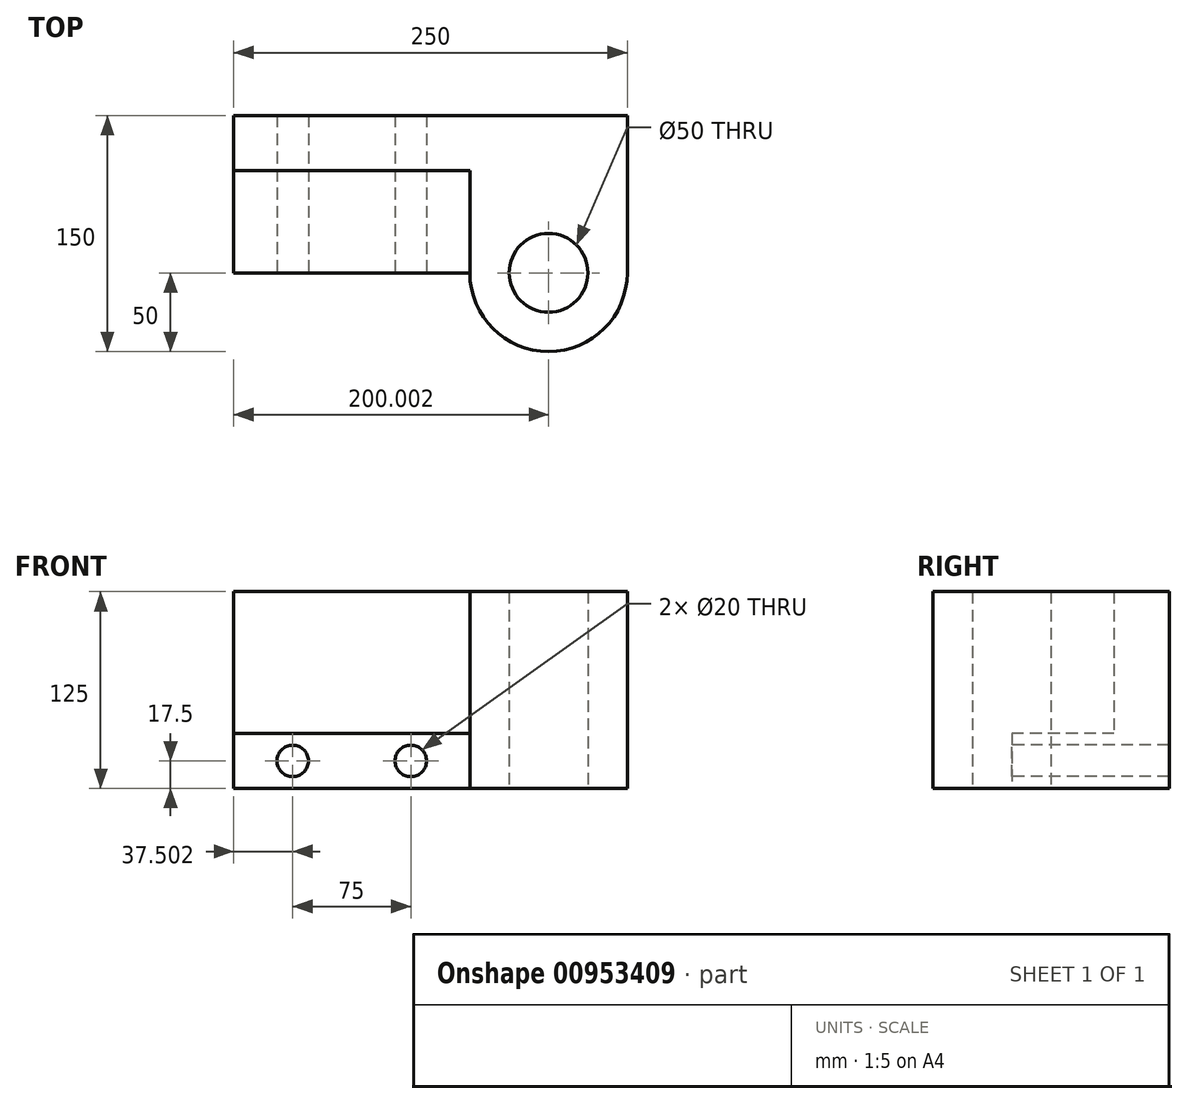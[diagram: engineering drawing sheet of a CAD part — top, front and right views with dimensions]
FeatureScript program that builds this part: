
annotation { "Feature Type Name" : "Feature", "Feature Type Description" : "" }
export const myFeature = defineFeature(function(context is Context, id is Id, definition is map)
    precondition{}
    {
        {
            var Q0;
            Q0=qCreatedBy(makeId("Top.planeOp"),FACE);
            var sketch = newSketch(context, id + "F0", { "sketchPlane" : qUnion([Q0])});
            skLineSegment(sketch, "E0", {"start": v(-118.58, 35) * mm, "end": v(131.42, 35) * mm});
            skLineSegment(sketch, "E1", {"start": v(-118.58, 35) * mm, "end": v(-118.58, 0) * mm});
            skLineSegment(sketch, "E2", {"start": v(-118.58, 0) * mm, "end": v(-118.58, -65) * mm});
            skLineSegment(sketch, "E3", {"start": v(-118.58, 0) * mm, "end": v(31.42, 0) * mm});
            skLineSegment(sketch, "E4", {"start": v(31.42, 0) * mm, "end": v(31.42, -65) * mm});
            skLineSegment(sketch, "E5", {"start": v(131.42, 35) * mm, "end": v(131.42, -65) * mm});
            skArc(sketch, "E6", {"start": v(31.42, -65) * mm, "mid": v(81.42, -115) * mm, "end": v(131.42, -65) * mm});
            skCircle(sketch, "E7", {"center": v(81.42, -65) * mm, "radius": 25 * mm});
            skLineSegment(sketch, "E8", {"start": v(-118.58, -65) * mm, "end": v(31.42, -65) * mm});
            skPoint(sketch, "E9.endSnap0", {"position": v(60.36, -110.35) * mm});
            skSolve(sketch);
        }
        {
            var Q0;
            Q0=makeQuery(id+"F0.imprint","IMPRINT",FACE,{"disambiguationData":[TD([[makeQuery(id+"F0.imprint","IMPRINT",EDGE,{"derivedFrom":sQuery(id+"F0.wireOp",EDGE,"E0")}),-1.0]])]});
            extrude(context, id + "F1", {"entities" : qUnion([Q0]), "depth" : 125 * mm, "offsetDistance" : 25 * mm});
        }
        {
            var Q0;
            Q0=makeQuery(id+"F0.imprint","IMPRINT",FACE,{"disambiguationData":[TD([[makeQuery(id+"F0.imprint","IMPRINT",EDGE,{"derivedFrom":sQuery(id+"F0.wireOp",EDGE,"E2")}),1.0]])]});
            extrude(context, id + "F2", {"entities" : qUnion([Q0]), "operationType" : NewBodyOperationType.ADD, "depth" : 35 * mm, "offsetDistance" : 25 * mm});
        }
        {
            var Q0;
            Q0=makeQuery(id+"F2.opExtrude","SWEPT_FACE",FACE,{"disambiguationData":[OSD([sQuery(id+"F0.wireOp",EDGE,"E8")])]});
            var sketch = newSketch(context, id + "F3", { "sketchPlane" : qUnion([Q0])});
            skCircle(sketch, "E10", {"center": v(-81.08, 17.5) * mm, "radius": 10 * mm});
            skCircle(sketch, "E11", {"center": v(-6.08, 17.5) * mm, "radius": 10 * mm});
            skSolve(sketch);
        }
        {
            var Q0;
            Q0=makeQuery(id+"F3.imprint","IMPRINT",FACE,{"disambiguationData":[TD([[makeQuery(id+"F3.imprint","IMPRINT",EDGE,{"derivedFrom":sQuery(id+"F3.wireOp",EDGE,"E10")}),1.0]])]});
            var Q1;
            Q1=makeQuery(id+"F3.imprint","IMPRINT",FACE,{"disambiguationData":[TD([[makeQuery(id+"F3.imprint","IMPRINT",EDGE,{"derivedFrom":sQuery(id+"F3.wireOp",EDGE,"E11")}),1.0]])]});
            extrude(context, id + "F4", {"entities" : qUnion([Q0, Q1]), "operationType" : NewBodyOperationType.REMOVE, "endBound" : BoundingType.THROUGH_ALL, "oppositeDirection" : true, "depth" : 25 * mm, "offsetDistance" : 25 * mm});
        }
    });
